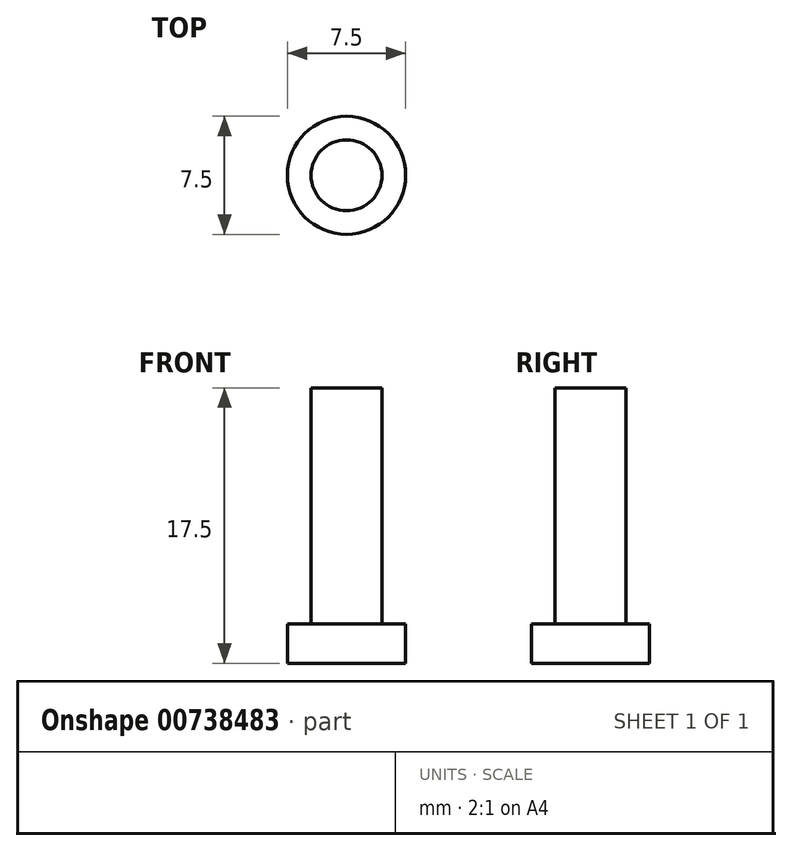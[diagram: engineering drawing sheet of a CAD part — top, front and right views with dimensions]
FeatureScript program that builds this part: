
annotation { "Feature Type Name" : "Feature", "Feature Type Description" : "" }
export const myFeature = defineFeature(function(context is Context, id is Id, definition is map)
    precondition{}
    {
        {
            var Q0;
            Q0=qCreatedBy(makeId("Top.planeOp"),FACE);
            var sketch = newSketch(context, id + "F0", { "sketchPlane" : qUnion([Q0])});
            skCircle(sketch, "E0", {"center": v(-4.18, 1.88) * mm, "radius": 3.76 * mm});
            skCircle(sketch, "E1", {"center": v(-4.18, 1.88) * mm, "radius": 2.25 * mm});
            skSolve(sketch);
        }
        {
            var Q0;
            Q0=makeQuery(id+"F0.imprint","IMPRINT",FACE,{"disambiguationData":[TD([[makeQuery(id+"F0.imprint","IMPRINT",EDGE,{"derivedFrom":sQuery(id+"F0.wireOp",EDGE,"E1")}),1.0]])]});
            extrude(context, id + "F1", {"entities" : qUnion([Q0]), "depth" : 17.5 * mm, "offsetDistance" : 25 * mm});
        }
        {
            var Q0;
            Q0=makeQuery(id+"F1.opExtrude","CAP_FACE",FACE,{"disambiguationData":[OSD([sQuery(id+"F0.wireOp",EDGE,"E1")])],"isStart":true});
            var sketch = newSketch(context, id + "F2", { "sketchPlane" : qUnion([Q0])});
            skCircle(sketch, "E2", {"center": v(-4.18, -1.88) * mm, "radius": 3.75 * mm});
            skSolve(sketch);
        }
        {
            var Q0;
            Q0=makeQuery(id+"F2.imprint","IMPRINT",FACE,{"disambiguationData":[TD([[makeQuery(id+"F2.imprint","IMPRINT",EDGE,{"derivedFrom":sQuery(id+"F2.wireOp",EDGE,"E2")}),1.0]])]});
            extrude(context, id + "F3", {"entities" : qUnion([Q0]), "operationType" : NewBodyOperationType.ADD, "oppositeDirection" : true, "depth" : 2.5 * mm, "offsetDistance" : 25 * mm});
        }
    });
